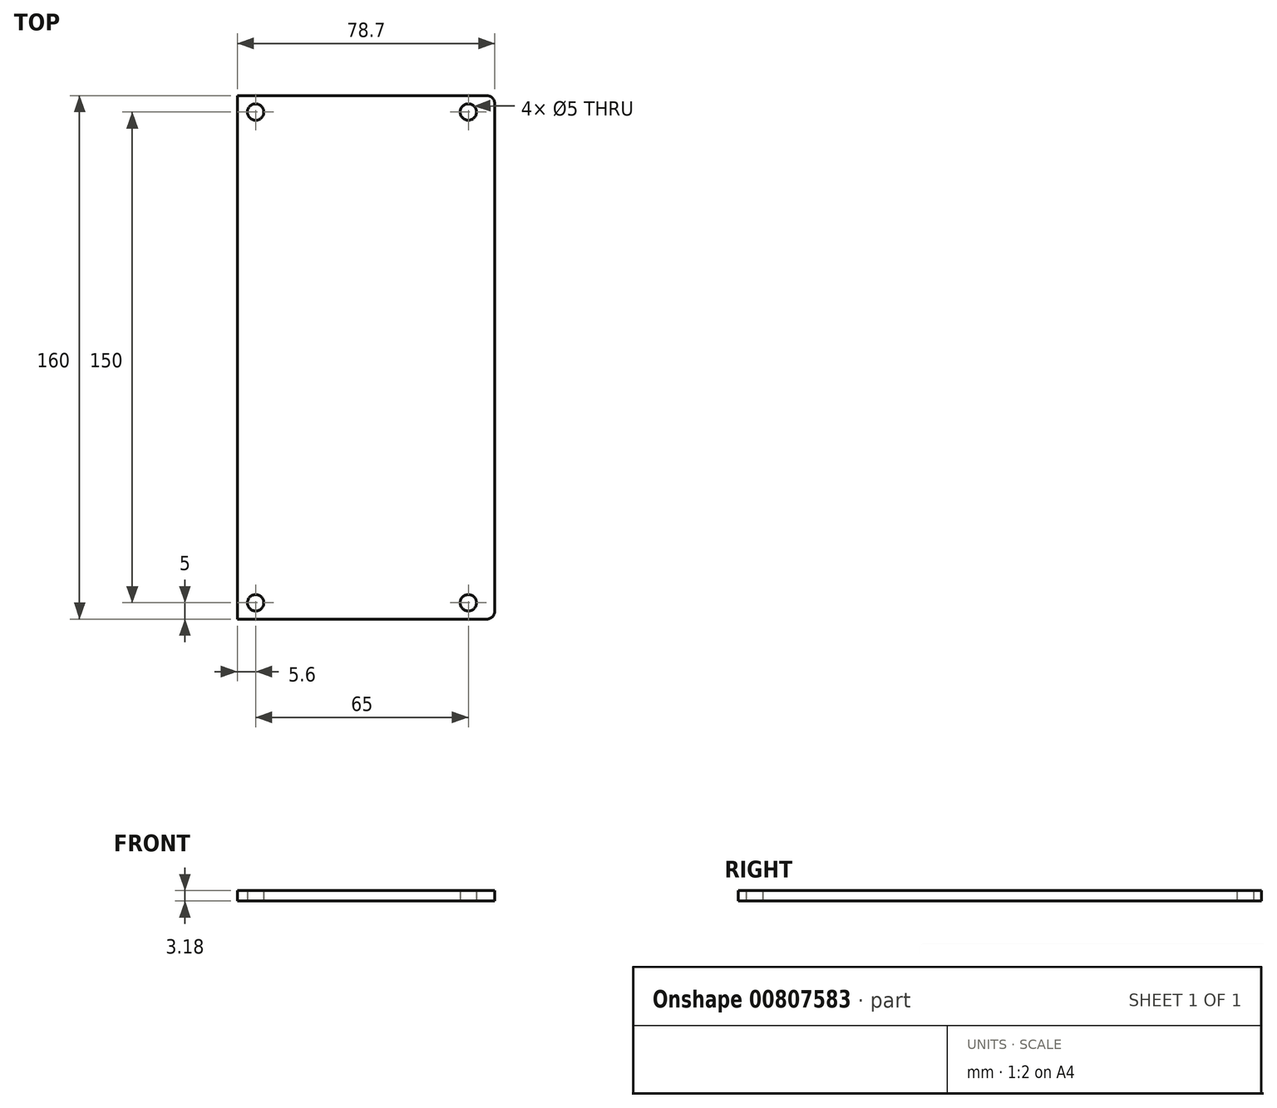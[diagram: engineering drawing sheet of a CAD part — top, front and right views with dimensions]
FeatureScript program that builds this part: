
annotation { "Feature Type Name" : "Feature", "Feature Type Description" : "" }
export const myFeature = defineFeature(function(context is Context, id is Id, definition is map)
    precondition{}
    {
        {
            var Q0;
            Q0=qCreatedBy(makeId("Top.planeOp"),FACE);
            var sketch = newSketch(context, id + "F0", { "sketchPlane" : qUnion([Q0])});
            skLineSegment(sketch, "E0.bottom", {"start": v(-32.5, 75) * mm, "end": v(32.5, 75) * mm, "construction": true});
            skLineSegment(sketch, "E0.top", {"start": v(-32.5, -75) * mm, "end": v(32.5, -75) * mm, "construction": true});
            skLineSegment(sketch, "E0.left", {"start": v(-32.5, 75) * mm, "end": v(-32.5, -75) * mm, "construction": true});
            skLineSegment(sketch, "E0.right", {"start": v(32.5, 75) * mm, "end": v(32.5, -75) * mm, "construction": true});
            skPoint(sketch, "E0.middle", {"position": v(0, 0) * mm});
            skCircle(sketch, "E1", {"center": v(-32.5, 75) * mm, "radius": 2.5 * mm});
            skCircle(sketch, "E2", {"center": v(32.5, 75) * mm, "radius": 2.5 * mm});
            skCircle(sketch, "E3", {"center": v(32.5, -75) * mm, "radius": 2.5 * mm});
            skCircle(sketch, "E4", {"center": v(-32.5, -75) * mm, "radius": 2.5 * mm});
            skLineSegment(sketch, "E5.bottom", {"start": v(-38.1, 80) * mm, "end": v(38.1, 80) * mm});
            skLineSegment(sketch, "E5.top", {"start": v(-38.1, -80) * mm, "end": v(38.1, -80) * mm});
            skLineSegment(sketch, "E5.left", {"start": v(-38.1, 80) * mm, "end": v(-38.1, -80) * mm});
            skLineSegment(sketch, "E6.bottom", {"start": v(38.1, 80) * mm, "end": v(38.1, 80) * mm});
            skLineSegment(sketch, "E6.top", {"start": v(38.1, -80) * mm, "end": v(38.1, -80) * mm});
            skLineSegment(sketch, "E6.left", {"start": v(38.1, 80) * mm, "end": v(38.1, -80) * mm, "construction": true});
            skLineSegment(sketch, "E6.right", {"start": v(40.6, 77.5) * mm, "end": v(40.6, -77.5) * mm});
            skPoint(sketch, "E7.visualSharp", {"position": v(40.6, 80) * mm});
            skArc(sketch, "E7.filletArc", {"start": v(40.6, 77.5) * mm, "mid": v(39.87, 79.27) * mm, "end": v(38.1, 80) * mm});
            skPoint(sketch, "E8.visualSharp", {"position": v(40.6, -80) * mm});
            skArc(sketch, "E8.filletArc", {"start": v(38.1, -80) * mm, "mid": v(39.87, -79.27) * mm, "end": v(40.6, -77.5) * mm});
            skSolve(sketch);
        }
        {
            var Q0;
            Q0=makeQuery(id+"F0.imprint","IMPRINT",FACE,{"disambiguationData":[TD([[makeQuery(id+"F0.imprint","IMPRINT",EDGE,{"derivedFrom":sQuery(id+"F0.wireOp",EDGE,"E1")}),-1.0]])]});
            extrude(context, id + "F1", {"entities" : qUnion([Q0]), "depth" : 3.17 * mm, "offsetDistance" : 25 * mm});
        }
    });
